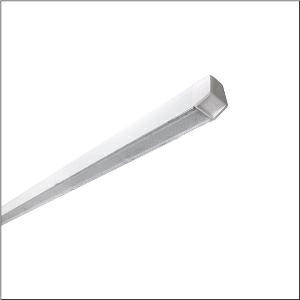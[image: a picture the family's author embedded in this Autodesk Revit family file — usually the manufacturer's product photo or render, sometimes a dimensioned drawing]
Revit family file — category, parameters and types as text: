
# Revit family: licross_r__21_recessed_ho_52ul1edv4k5r00s_c975
name_source: partatom
category: Lighting Fixtures
units: mm (PartAtom-declared; Revit-internal decimal feet)

## family parameters
Cut with Voids When Loaded = No
Host = Face
Light Source = No
Part Type = Normal
Room Calculation Point = No
Round Connector Dimension = Use Diameter
Shared = No

## types (1)
- --- (1 x LED, 19890 lm, 121.7 W, 4000K)
    Apparent Load = 122 VA
    CIE Flux Codes = 85 95 99 100 100
    Color Rendering = 80
    Color Temperature = 4000K
    Default Elevation = 1800 mm
    Description = Licross® 21 Recessed HO, single luminaire, primary optical cover: cover, of PMMA, light emission: direct distribution, primary light characteristic: symmetric, installation type: slip-in mounting, LED, rated luminous flux: 19.890lm, luminous efficacy: 163lm/W, light colour: 840, colour temperature: 4000K, control gear: ECG DALI, with terminal, 5-pole, max. 2.5mm², mains connection: 230V, AC, 50/60Hz, rated input power: 122W, Licross® LED insert, of sheet steel, galvanised, coil coated, white, with terminals, length: 2.327mm, width: 70mm, height: 71mm, end cap, of PC, white, mounting rail, of sheet steel, galvanised, white, protection rating (complete): IP20, insulation class (complete): insulation class I (protective earthing), certification: CE, ENEC, VDE, UKCA, impact resistance: IK06, permissible operating ambient temperature: -35..+30°C, corresponds to IFS (International Featured Standards) requirements for safety and quality in the food industry, reducing of maximum allowable ambient temperature of 5°C with ceiling mounting, LABS conformity tested according to VDMA 24364:2018-05, packaging unit: 1 piece
    Height = 58 mm
    Lamp = 1 x LED
    Lamp Light Flux = 19890 lm
    Lamp Power = 121.7 W
    Lamp count = 1
    Length = 2250 mm
    Luminous efficacy = 163 lm/W
    Manufacturer = Siteco
    ModVariant = No
    Model = 52UL1EDV4K5R00S
    Mounting Place = Ceiling
    Mounting Type = Pendant
    Number of Poles = 1
    OnlyDefault = Yes
    Power Factor = 1
    Product Name = Licross® 21 Recessed HO
    Product group = single luminaire
    ProductGroupID = 907
    Protection Class = Protection class I
    Protection Degree = IP 20
    RLX_Detail_Level = 1
    RLX_Emergency_Light_Flux = 0 lm
    RLX_Emergency_Type = 0
    RLX_Emergency_Type_DB = No
    RlxData = <blob elided: 31701 chars, md5=1cb1c442>
    Socket = socket
    Standby Power = 0 W
    System Light Flux = 19889 lm
    System Power = 122 W
    Type Comments = factory setting: luminous flux: 100 % | dim-lin: 254 | 490 mA
    Type Image = l_1006979.jpg
    URL = http://relux.com
    VarID = @adj_130847
    Voltage = 0 V
    Weight = 0.00 kg
    Width = 66 mm

## geometry (parser evidence)
native form markers: Blend x4, Sweep x8
no freeform markers — native parametric forms only
